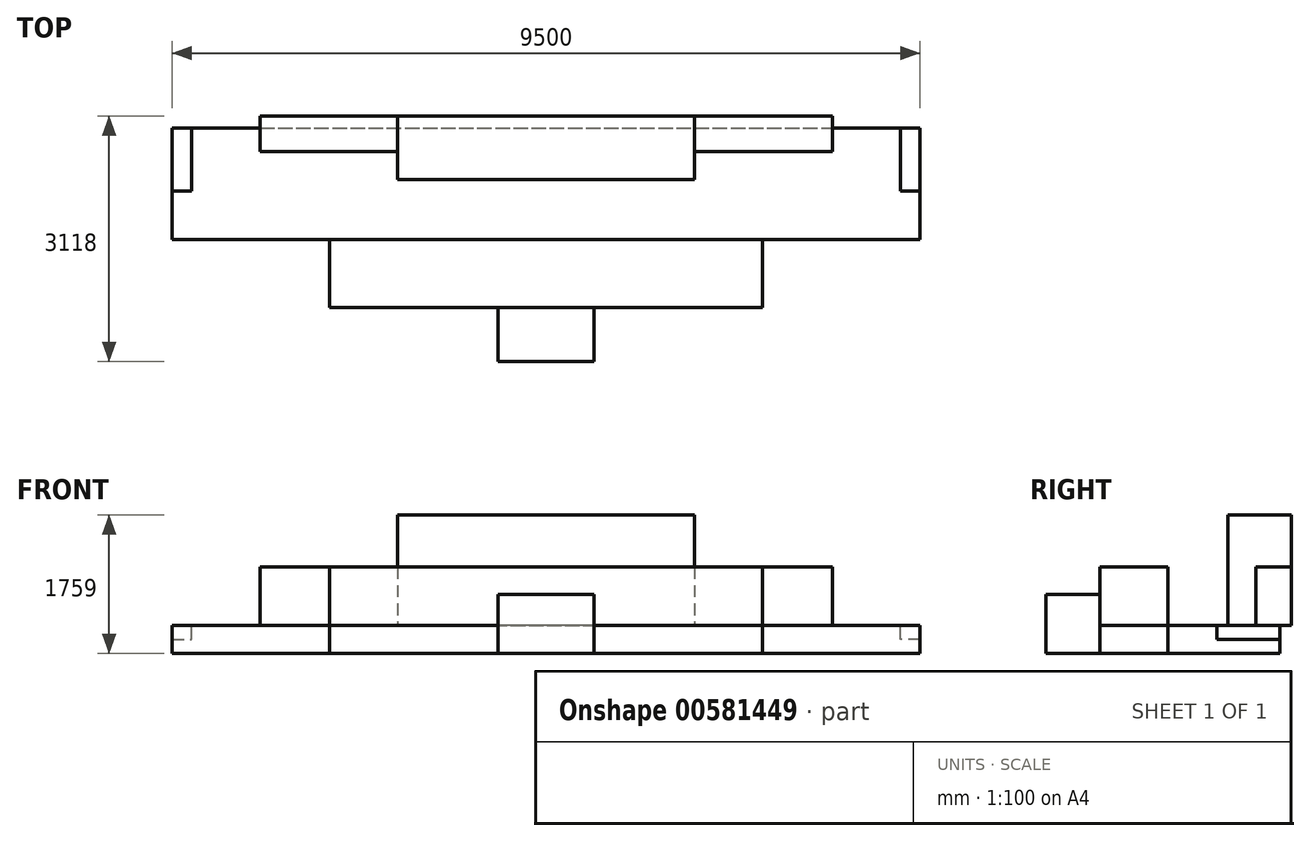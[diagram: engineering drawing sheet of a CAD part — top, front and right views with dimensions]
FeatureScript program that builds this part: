
annotation { "Feature Type Name" : "Feature", "Feature Type Description" : "" }
export const myFeature = defineFeature(function(context is Context, id is Id, definition is map)
    precondition{}
    {
        {
            var Q0;
            Q0=qCreatedBy(makeId("Right.planeOp"),FACE);
            var sketch = newSketch(context, id + "F0", { "sketchPlane" : qUnion([Q0])});
            skLineSegment(sketch, "E0.bottom", {"start": v(-1593, -1592) * mm, "end": v(-175, -1592) * mm});
            skLineSegment(sketch, "E0.top", {"start": v(-1593, -1950) * mm, "end": v(-175, -1950) * mm});
            skLineSegment(sketch, "E0.left", {"start": v(-1593, -1592) * mm, "end": v(-1593, -1950) * mm});
            skLineSegment(sketch, "E0.right", {"start": v(-175, -1592) * mm, "end": v(-175, -1950) * mm});
            skLineSegment(sketch, "E1", {"start": v(0, 0) * mm, "end": v(0, -1950) * mm, "construction": true});
            skLineSegment(sketch, "E2", {"start": v(0, -1950) * mm, "end": v(-1979.79, -1950) * mm, "construction": true});
            skSolve(sketch);
        }
        {
            var Q0;
            Q0=qSketchRegion(id+"F0",true);
            extrude(context, id + "F1", {"entities" : qUnion([Q0]), "oppositeDirection" : true, "depth" : 4750 * mm, "offsetDistance" : 25 * mm});
        }
        {
            var Q0;
            Q0=makeQuery(id+"F1.opExtrude","SWEPT_BODY",BODY,{"disambiguationData":[OSD([sQuery(id+"F0.wireOp",EDGE,"E0.bottom"),sQuery(id+"F0.wireOp",EDGE,"E0.top"),sQuery(id+"F0.wireOp",EDGE,"E0.left"),sQuery(id+"F0.wireOp",EDGE,"E0.right")])]});
            var Q1;
            Q1=makeQuery(id+"F1.opExtrude","CAP_FACE",FACE,{"disambiguationData":[OSD([sQuery(id+"F0.wireOp",EDGE,"E0.bottom"),sQuery(id+"F0.wireOp",EDGE,"E0.top"),sQuery(id+"F0.wireOp",EDGE,"E0.left"),sQuery(id+"F0.wireOp",EDGE,"E0.right")])],"isStart":true});
            mirror(context, id + "F2", {"entities" : qUnion([Q0]), "mirrorPlane" : qUnion([Q1])});
        }
        {
            var Q0;
            Q0=makeQuery(id+"F1.opExtrude","SWEPT_FACE",FACE,{"disambiguationData":[OSD([sQuery(id+"F0.wireOp",EDGE,"E0.bottom")])]});
            var sketch = newSketch(context, id + "F3", { "sketchPlane" : qUnion([Q0])});
            skLineSegment(sketch, "E3.bottom", {"start": v(1884.5, -25) * mm, "end": v(-1884.5, -25) * mm});
            skLineSegment(sketch, "E3.top", {"start": v(1884.5, -831) * mm, "end": v(-1884.5, -831) * mm});
            skLineSegment(sketch, "E3.left", {"start": v(1884.5, -25) * mm, "end": v(1884.5, -831) * mm});
            skLineSegment(sketch, "E3.right", {"start": v(-1884.5, -25) * mm, "end": v(-1884.5, -831) * mm});
            skPoint(sketch, "E3.middle", {"position": v(0, -428) * mm});
            skLineSegment(sketch, "E4.top", {"start": v(2750, -2457) * mm, "end": v(-2750, -2457) * mm});
            skLineSegment(sketch, "E4.left", {"start": v(2750, -1593) * mm, "end": v(2750, -2457) * mm});
            skLineSegment(sketch, "E4.right", {"start": v(-2750, -1593) * mm, "end": v(-2750, -2457) * mm});
            skPoint(sketch, "E4.middle", {"position": v(0, -2025) * mm});
            skLineSegment(sketch, "E5.bottom", {"start": v(610, -3143) * mm, "end": v(-610, -3143) * mm});
            skLineSegment(sketch, "E5.top", {"start": v(610, -2457) * mm, "end": v(-610, -2457) * mm});
            skLineSegment(sketch, "E5.left", {"start": v(610, -3143) * mm, "end": v(610, -2457) * mm});
            skLineSegment(sketch, "E5.right", {"start": v(-610, -3143) * mm, "end": v(-610, -2457) * mm});
            skPoint(sketch, "E5.middle", {"position": v(0, -2800) * mm});
            skPoint(sketch, "E5.middle.positionSnap0", {"position": v(0, -2457) * mm});
            skPoint(sketch, "E5.centerSnap0", {"position": v(0, -2457) * mm});
            skLineSegment(sketch, "E6", {"start": v(-2750, -1593) * mm, "end": v(2750, -1593) * mm});
            skLineSegment(sketch, "E7.bottom", {"start": v(1884.5, -25) * mm, "end": v(3634.5, -25) * mm});
            skLineSegment(sketch, "E7.top", {"start": v(1884.5, -475) * mm, "end": v(3634.5, -475) * mm});
            skLineSegment(sketch, "E7.left", {"start": v(1884.5, -25) * mm, "end": v(1884.5, -475) * mm});
            skLineSegment(sketch, "E7.right", {"start": v(3634.5, -25) * mm, "end": v(3634.5, -475) * mm});
            skPoint(sketch, "E8.oppositeSnap0", {"position": v(-1884.5, -428) * mm});
            skLineSegment(sketch, "E9.bottom", {"start": v(-1884.5, -25) * mm, "end": v(-3634.5, -25) * mm});
            skLineSegment(sketch, "E9.top", {"start": v(-1884.5, -475) * mm, "end": v(-3634.5, -475) * mm});
            skLineSegment(sketch, "E9.left", {"start": v(-1884.5, -25) * mm, "end": v(-1884.5, -475) * mm});
            skLineSegment(sketch, "E9.right", {"start": v(-3634.5, -25) * mm, "end": v(-3634.5, -475) * mm});
            skSolve(sketch);
        }
        {
            var Q0;
            {var subQ0=sQuery(id+"F3.wireOp",EDGE,"E3.right");Q0=makeQuery(id+"F3.imprint","IMPRINT",FACE,{"disambiguationData":[TD([[makeQuery(id+"F3.imprint","IMPRINT",EDGE,{"derivedFrom":subQ0}),1.0]])]});}
            var Q1;
            {var subQ0=sQuery(id+"F3.wireOp",EDGE,"E3.left");Q1=makeQuery(id+"F3.imprint","IMPRINT",FACE,{"disambiguationData":[TD([[makeQuery(id+"F3.imprint","IMPRINT",EDGE,{"derivedFrom":subQ0}),-1.0]])]});}
            extrude(context, id + "F4", {"entities" : qUnion([Q0, Q1]), "depth" : 1400 * mm, "offsetDistance" : 25 * mm});
        }
        {
            var Q0;
            {var subQ0=sQuery(id+"F3.wireOp",EDGE,"E6");var subQ1=sQuery(id+"F3.wireOp",EDGE,"E4.right");var subQ2=makeQuery(id+"F3.imprint","INTERSECT",VERTEX,{"derivedFrom":[subQ1,subQ0]});Q0=makeQuery(id+"F3.imprint","IMPRINT",FACE,{"disambiguationData":[TD([[makeQuery(id+"F3.imprint","IMPRINT",EDGE,{"disambiguationData":[TD([[subQ2,-1.0]])],"derivedFrom":subQ0}),-1.0]])]});}
            var Q1;
            {var subQ6=sQuery(id+"F3.wireOp",EDGE,"E4.left");Q1=makeQuery(id+"F3.imprint","IMPRINT",FACE,{"disambiguationData":[TD([[makeQuery(id+"F3.imprint","IMPRINT",EDGE,{"derivedFrom":subQ6}),-1.0]])]});}
            extrude(context, id + "F5", {"entities" : qUnion([Q0, Q1]), "depth" : 737 * mm, "offsetDistance" : 25 * mm});
        }
        {
            var Q0;
            Q0=makeQuery(id+"F3.imprint","IMPRINT",FACE,{"disambiguationData":[TD([[makeQuery(id+"F3.imprint","IMPRINT",EDGE,{"derivedFrom":sQuery(id+"F3.wireOp",EDGE,"E5.bottom")}),-1.0]])]});
            extrude(context, id + "F6", {"entities" : qUnion([Q0]), "depth" : 390 * mm, "offsetDistance" : 25 * mm});
        }
        {
            var Q0;
            Q0=makeQuery(id+"F3.imprint","IMPRINT",FACE,{"disambiguationData":[TD([[makeQuery(id+"F3.imprint","IMPRINT",EDGE,{"derivedFrom":sQuery(id+"F3.wireOp",EDGE,"E5.bottom")}),-1.0]])]});
            extrude(context, id + "F7", {"entities" : qUnion([Q0]), "operationType" : NewBodyOperationType.ADD, "oppositeDirection" : true, "depth" : 359 * mm, "offsetDistance" : 25 * mm});
        }
        {
            var Q0;
            {var subQ1=sQuery(id+"F3.wireOp",EDGE,"E4.left");Q0=makeQuery(id+"F3.imprint","IMPRINT",FACE,{"disambiguationData":[TD([[makeQuery(id+"F3.imprint","IMPRINT",EDGE,{"derivedFrom":subQ1}),-1.0]])]});}
            extrude(context, id + "F8", {"entities" : qUnion([Q0]), "oppositeDirection" : true, "depth" : 359 * mm, "offsetDistance" : 25 * mm});
        }
        {
            var Q0;
            Q0=makeQuery(id+"F1.opExtrude","SWEPT_BODY",BODY,{"disambiguationData":[OSD([sQuery(id+"F0.wireOp",EDGE,"E0.bottom"),sQuery(id+"F0.wireOp",EDGE,"E0.top"),sQuery(id+"F0.wireOp",EDGE,"E0.left"),sQuery(id+"F0.wireOp",EDGE,"E0.right")])]});
            var Q1;
            Q1=makeQuery(id+"F2.opPattern","COPY",BODY,{"derivedFrom":makeQuery(id+"F1.opExtrude","SWEPT_BODY",BODY,{"disambiguationData":[OSD([sQuery(id+"F0.wireOp",EDGE,"E0.bottom"),sQuery(id+"F0.wireOp",EDGE,"E0.top"),sQuery(id+"F0.wireOp",EDGE,"E0.left"),sQuery(id+"F0.wireOp",EDGE,"E0.right")])]}),"instanceName":"1"});
            var Q2;
            Q2=makeQuery(id+"F8.opExtrude","SWEPT_BODY",BODY,{"disambiguationData":[OSD([sQuery(id+"F3.wireOp",EDGE,"E4.top"),sQuery(id+"F3.wireOp",EDGE,"E4.left"),sQuery(id+"F3.wireOp",EDGE,"E4.right"),sQuery(id+"F3.wireOp",EDGE,"E5.top"),sQuery(id+"F3.wireOp",EDGE,"E6")])]});
            booleanBodies(context, id + "F9", {"operationType" : BooleanOperationType.UNION, "tools" : qUnion([Q0, Q1, Q2])});
        }
        {
            var Q0;
            {var subQ0=makeQuery(id+"F1.opExtrude","SWEPT_FACE",FACE,{"disambiguationData":[OSD([sQuery(id+"F0.wireOp",EDGE,"E0.right")])]});Q0=makeQuery(id+"F9.opBoolean","MERGE",FACE,{"derivedFrom":[subQ0,makeQuery(id+"F2.opPattern","COPY",FACE,{"derivedFrom":subQ0,"instanceName":"1"})]});}
            var sketch = newSketch(context, id + "F10", { "sketchPlane" : qUnion([Q0])});
            skLineSegment(sketch, "E10.0.3", {"start": v(4750, -1771) * mm, "end": v(4750, -1592) * mm});
            skLineSegment(sketch, "E11", {"start": v(4750, -1771) * mm, "end": v(4500, -1771) * mm});
            skLineSegment(sketch, "E12", {"start": v(4500, -1771) * mm, "end": v(4500, -1592) * mm});
            skPoint(sketch, "E13.orphan", {"position": v(4750, -1950) * mm});
            skLineSegment(sketch, "E14", {"start": v(4750, -1592) * mm, "end": v(4500, -1592) * mm});
            skLineSegment(sketch, "E15", {"start": v(0, 0) * mm, "end": v(0, -3084.56) * mm, "construction": true});
            skLineSegment(sketch, "E16.MirrorCS", {"start": v(-4750, -1771) * mm, "end": v(-4750, -1592) * mm});
            skPoint(sketch, "E17.MirrorP", {"position": v(-4750, -1950) * mm});
            skLineSegment(sketch, "E18.MirrorCS", {"start": v(-4750, -1592) * mm, "end": v(-4500, -1592) * mm});
            skLineSegment(sketch, "E19.MirrorCS", {"start": v(-4750, -1771) * mm, "end": v(-4500, -1771) * mm});
            skLineSegment(sketch, "E20.MirrorCS", {"start": v(-4500, -1771) * mm, "end": v(-4500, -1592) * mm});
            skSolve(sketch);
        }
        {
            var Q0;
            Q0=makeQuery(id+"F10.imprint","IMPRINT",FACE,{"disambiguationData":[TD([[makeQuery(id+"F10.imprint","IMPRINT",EDGE,{"derivedFrom":sQuery(id+"F10.wireOp",EDGE,"E10.0.3")}),-1.0]])]});
            var Q1;
            Q1=makeQuery(id+"F10.imprint","IMPRINT",FACE,{"disambiguationData":[TD([[makeQuery(id+"F10.imprint","IMPRINT",EDGE,{"derivedFrom":sQuery(id+"F10.wireOp",EDGE,"E18.MirrorCS")}),1.0]])]});
            extrude(context, id + "F11", {"entities" : qUnion([Q0, Q1]), "operationType" : NewBodyOperationType.REMOVE, "oppositeDirection" : true, "depth" : 800 * mm, "offsetDistance" : 25 * mm});
        }
        {
            var Q0;
            Q0=makeQuery(id+"F3.imprint","IMPRINT",FACE,{"disambiguationData":[TD([[makeQuery(id+"F3.imprint","IMPRINT",EDGE,{"derivedFrom":sQuery(id+"F3.wireOp",EDGE,"E7.bottom")}),-1.0]])]});
            var Q1;
            {var subQ0=sQuery(id+"F3.wireOp",EDGE,"E9.top");Q1=makeQuery(id+"F3.imprint","IMPRINT",FACE,{"disambiguationData":[TD([[makeQuery(id+"F3.imprint","IMPRINT",EDGE,{"derivedFrom":subQ0}),-1.0]])]});}
            var Q2;
            {var subQ0=sQuery(id+"F3.wireOp",EDGE,"E9.bottom");Q2=makeQuery(id+"F3.imprint","IMPRINT",FACE,{"disambiguationData":[TD([[makeQuery(id+"F3.imprint","IMPRINT",EDGE,{"derivedFrom":subQ0}),1.0]])]});}
            extrude(context, id + "F12", {"entities" : qUnion([Q0, Q1, Q2]), "operationType" : NewBodyOperationType.ADD, "depth" : 737 * mm, "offsetDistance" : 25 * mm});
        }
    });
